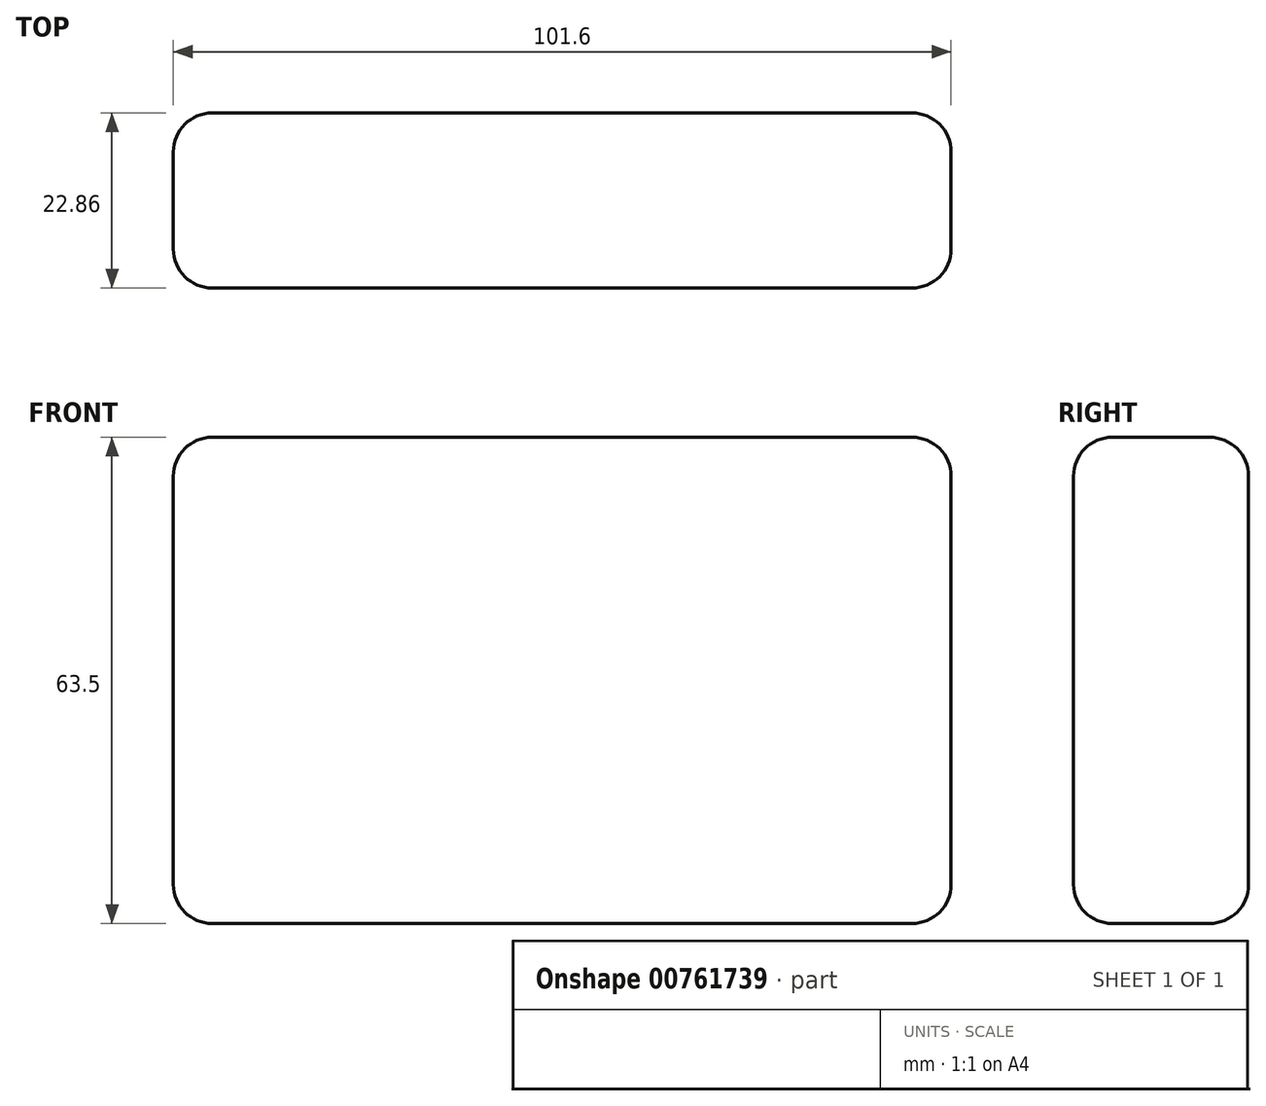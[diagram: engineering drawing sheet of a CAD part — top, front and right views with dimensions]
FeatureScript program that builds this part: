
annotation { "Feature Type Name" : "Feature", "Feature Type Description" : "" }
export const myFeature = defineFeature(function(context is Context, id is Id, definition is map)
    precondition{}
    {
        {
            var Q0;
            Q0=qCreatedBy(makeId("Front.planeOp"),FACE);
            var sketch = newSketch(context, id + "F0", { "sketchPlane" : qUnion([Q0])});
            skLineSegment(sketch, "E0.bottom", {"start": v(-54.82, 28.53) * mm, "end": v(46.78, 28.53) * mm});
            skLineSegment(sketch, "E0.top", {"start": v(-54.82, -34.97) * mm, "end": v(46.78, -34.97) * mm});
            skLineSegment(sketch, "E0.left", {"start": v(-54.82, 28.53) * mm, "end": v(-54.82, -34.97) * mm});
            skLineSegment(sketch, "E0.right", {"start": v(46.78, 28.53) * mm, "end": v(46.78, -34.97) * mm});
            skSolve(sketch);
        }
        {
            var Q0;
            Q0=makeQuery(id+"F0.imprint","IMPRINT",FACE,{"disambiguationData":[TD([[makeQuery(id+"F0.imprint","IMPRINT",EDGE,{"derivedFrom":sQuery(id+"F0.wireOp",EDGE,"E0.bottom")}),-1.0]])]});
            extrude(context, id + "F1", {"entities" : qUnion([Q0]), "depth" : 22.86 * mm, "offsetDistance" : 25.4 * mm});
        }
        {
            var Q0;
            Q0=makeQuery(id+"F1.opExtrude","SWEPT_FACE",FACE,{"disambiguationData":[OSD([sQuery(id+"F0.wireOp",EDGE,"E0.bottom")])]});
            var Q1;
            Q1=makeQuery(id+"F1.opExtrude","SWEPT_FACE",FACE,{"disambiguationData":[OSD([sQuery(id+"F0.wireOp",EDGE,"E0.right")])]});
            var Q2;
            Q2=makeQuery(id+"F1.opExtrude","SWEPT_FACE",FACE,{"disambiguationData":[OSD([sQuery(id+"F0.wireOp",EDGE,"E0.left")])]});
            var Q3;
            Q3=makeQuery(id+"F1.opExtrude","SWEPT_FACE",FACE,{"disambiguationData":[OSD([sQuery(id+"F0.wireOp",EDGE,"E0.top")])]});
            fillet(context, id + "F2", {"entities" : qUnion([Q0, Q1, Q2, Q3]), "radius" : 5.08 * mm, "tangentPropagation" : true, "allowEdgeOverflow" : false});
        }
    });
